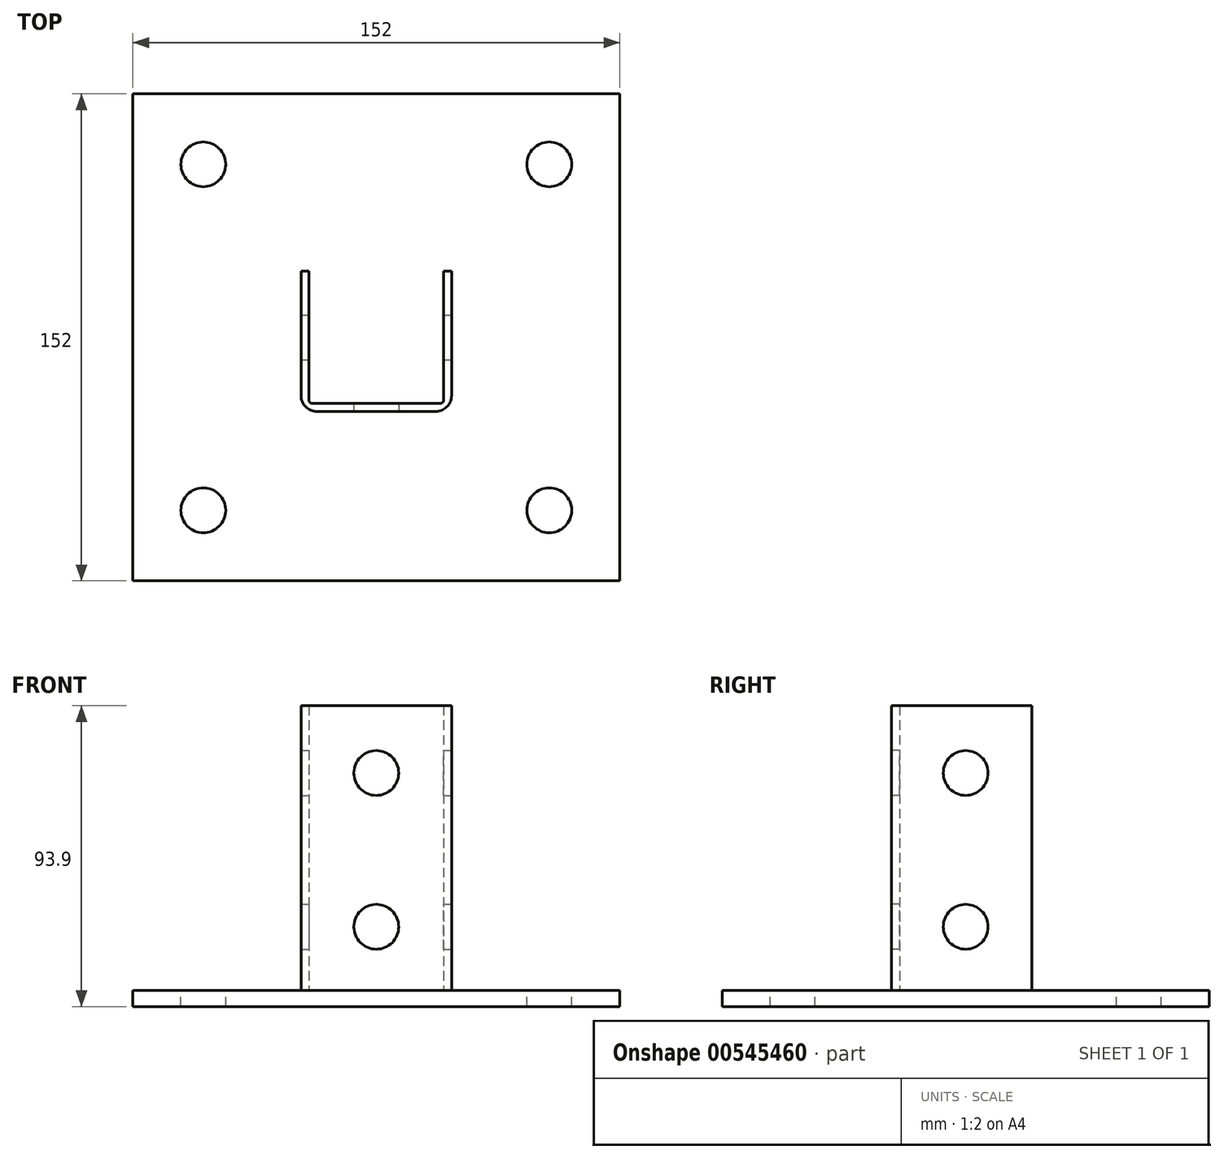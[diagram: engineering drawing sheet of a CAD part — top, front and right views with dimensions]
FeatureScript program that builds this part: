
annotation { "Feature Type Name" : "Feature", "Feature Type Description" : "" }
export const myFeature = defineFeature(function(context is Context, id is Id, definition is map)
    precondition{}
    {
        {
            var Q0;
            Q0=qCreatedBy(makeId("Top.planeOp"),FACE);
            var sketch = newSketch(context, id + "F0", { "sketchPlane" : qUnion([Q0])});
            skLineSegment(sketch, "E0.bottom", {"start": v(-76, 76) * mm, "end": v(76, 76) * mm});
            skLineSegment(sketch, "E0.top", {"start": v(-76, -76) * mm, "end": v(76, -76) * mm});
            skLineSegment(sketch, "E0.left", {"start": v(-76, 76) * mm, "end": v(-76, -76) * mm});
            skLineSegment(sketch, "E0.right", {"start": v(76, 76) * mm, "end": v(76, -76) * mm});
            skCircle(sketch, "E1", {"center": v(-54, 54) * mm, "radius": 7 * mm});
            skCircle(sketch, "E2", {"center": v(54, 54) * mm, "radius": 7 * mm});
            skCircle(sketch, "E3", {"center": v(-54, -54) * mm, "radius": 7 * mm});
            skCircle(sketch, "E4", {"center": v(54, -54) * mm, "radius": 7 * mm});
            skSolve(sketch);
        }
        {
            var Q0;
            Q0=makeQuery(id+"F0.imprint","IMPRINT",FACE,{"disambiguationData":[TD([[makeQuery(id+"F0.imprint","IMPRINT",EDGE,{"derivedFrom":sQuery(id+"F0.wireOp",EDGE,"E0.bottom")}),-1.0]])]});
            extrude(context, id + "F1", {"entities" : qUnion([Q0]), "oppositeDirection" : true, "depth" : 5 * mm, "offsetDistance" : 25 * mm});
        }
        {
            var Q0;
            Q0=makeQuery(id+"F1.opExtrude","CAP_FACE",FACE,{"disambiguationData":[OSD([sQuery(id+"F0.wireOp",EDGE,"E0.bottom"),sQuery(id+"F0.wireOp",EDGE,"E0.top"),sQuery(id+"F0.wireOp",EDGE,"E0.left"),sQuery(id+"F0.wireOp",EDGE,"E0.right")])],"isStart":true});
            var sketch = newSketch(context, id + "F2", { "sketchPlane" : qUnion([Q0])});
            skLineSegment(sketch, "E5", {"start": v(-23.5, 20.65) * mm, "end": v(-23.5, -23.15) * mm});
            skLineSegment(sketch, "E6", {"start": v(-23.5, -23.15) * mm, "end": v(23.5, -23.15) * mm});
            skLineSegment(sketch, "E7", {"start": v(23.5, -23.15) * mm, "end": v(23.5, 20.65) * mm});
            skLineSegment(sketch, "E8", {"start": v(23.5, 20.65) * mm, "end": v(21, 20.65) * mm});
            skLineSegment(sketch, "E9", {"start": v(21, 20.65) * mm, "end": v(21, -20.65) * mm});
            skLineSegment(sketch, "E10", {"start": v(21, -20.65) * mm, "end": v(-21, -20.65) * mm});
            skLineSegment(sketch, "E11", {"start": v(-21, -20.65) * mm, "end": v(-21, 20.65) * mm});
            skLineSegment(sketch, "E12", {"start": v(-21, 20.65) * mm, "end": v(-23.5, 20.65) * mm});
            skSolve(sketch);
        }
        {
            var Q0;
            Q0=qSketchRegion(id+"F2",true);
            extrude(context, id + "F3", {"entities" : qUnion([Q0]), "operationType" : NewBodyOperationType.ADD, "depth" : 88.9 * mm, "offsetDistance" : 25 * mm});
        }
        {
            var Q0;
            Q0=makeQuery(id+"F3.opExtrude","SWEPT_EDGE",EDGE,{"disambiguationData":[OSD([sQuery(id+"F2.wireOp",EDGE,"E6"),sQuery(id+"F2.wireOp",EDGE,"E7")])]});
            var Q1;
            Q1=makeQuery(id+"F3.opExtrude","SWEPT_EDGE",EDGE,{"disambiguationData":[OSD([sQuery(id+"F2.wireOp",EDGE,"E5"),sQuery(id+"F2.wireOp",EDGE,"E6")])]});
            fillet(context, id + "F4", {"entities" : qUnion([Q0, Q1]), "radius" : 5 * mm, "tangentPropagation" : true, "allowEdgeOverflow" : false});
        }
        {
            var Q0;
            Q0=makeQuery(id+"F3.opExtrude","SWEPT_EDGE",EDGE,{"disambiguationData":[OSD([sQuery(id+"F2.wireOp",EDGE,"E9"),sQuery(id+"F2.wireOp",EDGE,"E10")])]});
            var Q1;
            Q1=makeQuery(id+"F3.opExtrude","SWEPT_EDGE",EDGE,{"disambiguationData":[OSD([sQuery(id+"F2.wireOp",EDGE,"E10"),sQuery(id+"F2.wireOp",EDGE,"E11")])]});
            fillet(context, id + "F5", {"entities" : qUnion([Q0, Q1]), "radius" : 1 * mm, "tangentPropagation" : true, "allowEdgeOverflow" : false});
        }
        {
            var Q0;
            Q0=makeQuery(id+"F3.opExtrude","SWEPT_FACE",FACE,{"disambiguationData":[OSD([sQuery(id+"F2.wireOp",EDGE,"E7")])]});
            var sketch = newSketch(context, id + "F6", { "sketchPlane" : qUnion([Q0])});
            skCircle(sketch, "E13", {"center": v(0, 67.9) * mm, "radius": 7 * mm});
            skCircle(sketch, "E14", {"center": v(0, 19.9) * mm, "radius": 5.94 * mm});
            skSolve(sketch);
        }
        {
            var Q0;
            Q0=sQuery(id+"F6.wireOp",VERTEX,"E13.center");
            var Q1;
            Q1=sQuery(id+"F6.wireOp",VERTEX,"E14.center");
            var Q2;
            Q2=makeQuery(id+"F1.opExtrude","SWEPT_BODY",BODY,{"disambiguationData":[OSD([sQuery(id+"F0.wireOp",EDGE,"E0.bottom"),sQuery(id+"F0.wireOp",EDGE,"E0.top"),sQuery(id+"F0.wireOp",EDGE,"E0.left"),sQuery(id+"F0.wireOp",EDGE,"E0.right"),sQuery(id+"F0.wireOp",EDGE,"E1"),sQuery(id+"F0.wireOp",EDGE,"E2"),sQuery(id+"F0.wireOp",EDGE,"E3"),sQuery(id+"F0.wireOp",EDGE,"E4")])]});
            hole(context, id + "F7", {"style" : HoleStyle.SIMPLE, "endStyle" : HoleEndStyle.THROUGH, "holeDiameter" : 14 * mm, "tappedDepth" : 12 * mm, "tapClearance" : 3, "locations" : qUnion([Q0, Q1]), "scope" : qUnion([Q2])});
        }
        {
            var Q0;
            Q0=makeQuery(id+"F3.opExtrude","SWEPT_FACE",FACE,{"disambiguationData":[OSD([sQuery(id+"F2.wireOp",EDGE,"E6")])]});
            var sketch = newSketch(context, id + "F8", { "sketchPlane" : qUnion([Q0])});
            skCircle(sketch, "E15", {"center": v(0, 67.9) * mm, "radius": 5.73 * mm});
            skCircle(sketch, "E16", {"center": v(0, 19.9) * mm, "radius": 6.4 * mm});
            skSolve(sketch);
        }
        {
            var Q0;
            Q0=sQuery(id+"F8.wireOp",VERTEX,"QaGs6MCo-ojgY-4r94-5WBR-ikx6SOWGX9Km.center");
            var Q1;
            Q1=sQuery(id+"F8.wireOp",VERTEX,"E15.center");
            var Q2;
            Q2=sQuery(id+"F8.wireOp",VERTEX,"E16.center");
            var Q3;
            Q3=makeQuery(id+"F1.opExtrude","SWEPT_BODY",BODY,{"disambiguationData":[OSD([sQuery(id+"F0.wireOp",EDGE,"E0.bottom"),sQuery(id+"F0.wireOp",EDGE,"E0.top"),sQuery(id+"F0.wireOp",EDGE,"E0.left"),sQuery(id+"F0.wireOp",EDGE,"E0.right"),sQuery(id+"F0.wireOp",EDGE,"E1"),sQuery(id+"F0.wireOp",EDGE,"E2"),sQuery(id+"F0.wireOp",EDGE,"E3"),sQuery(id+"F0.wireOp",EDGE,"E4")])]});
            hole(context, id + "F9", {"style" : HoleStyle.SIMPLE, "endStyle" : HoleEndStyle.THROUGH, "holeDiameter" : 14 * mm, "tappedDepth" : 12 * mm, "tapClearance" : 3, "locations" : qUnion([Q0, Q1, Q2]), "scope" : qUnion([Q3])});
        }
    });
